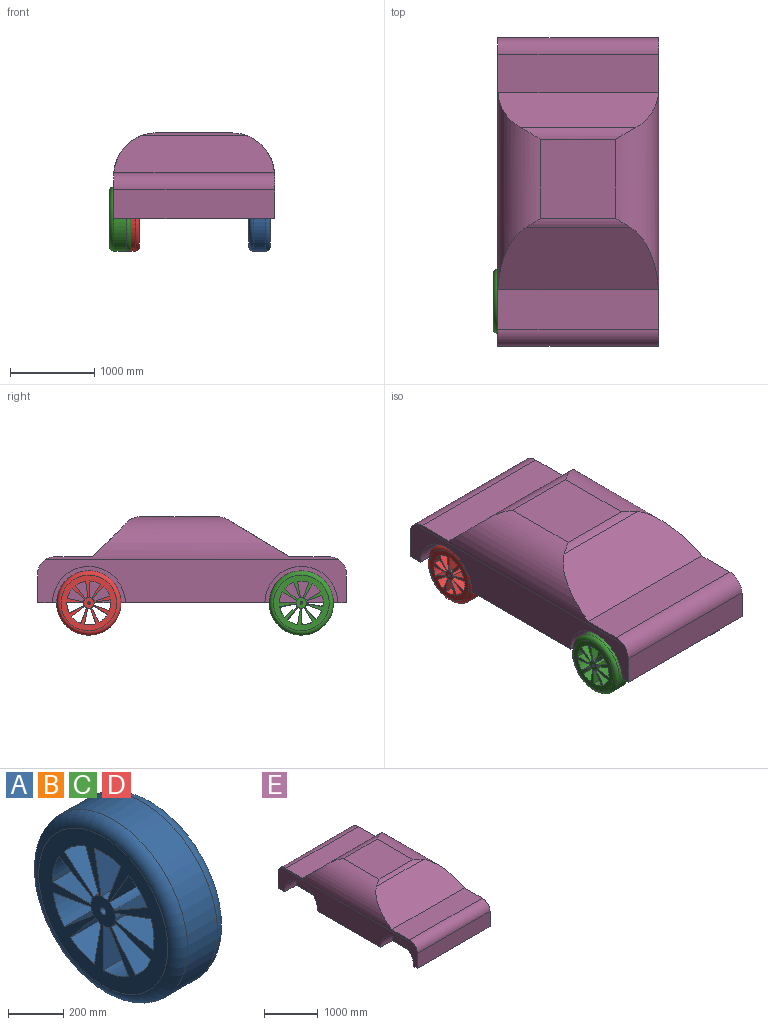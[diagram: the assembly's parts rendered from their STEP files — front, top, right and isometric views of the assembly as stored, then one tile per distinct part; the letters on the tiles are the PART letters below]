
ASSEMBLY  parts=5 mates=9
PART A: 42 faces, bbox 254x824.8x824.8 mm
  f0: plane 660.4x660.4mm, normal (1,0,0), area 191964.8mm2, adj f2,f5,f6,f7,f8,f9,f10,f11
  f1: plane 660.4x660.4mm, normal (-1,0,0), area 191964.8mm2, adj f2,f4,f6,f7,f8,f9,f10,f11
  f2: cylinder r=14.29mm len=254mm, axis (-1,0,0), area 22801.8mm2, adj f0,f1
  f3: cylinder r=381mm len=762mm, axis (-1,0,0), area 364829.4mm2, adj f4,f5
  f4: torus R=330.2mm, axis (1,0,0), area 181769mm2, adj f1,f3
  f5: torus R=330.2mm, axis (1,0,0), area 181769mm2, adj f0,f3
  f6: cylinder r=63.5mm len=254mm, axis (-1,0,0), area 8445.1mm2, adj f0,f1,f7,f9
  f7: plane 254x170.28mm, normal (0,0.5,-0.87), area 49942.1mm2, adj f0,f1,f6,f8
  f8: cylinder r=260.12mm len=254mm, axis (-1,0,0), area 34594.8mm2, adj f0,f1,f7,f9
  f9: plane 254x196.62mm, normal (0,0,1), area 49942.1mm2, adj f0,f1,f6,f8
  f10: plane 254x184.76mm, normal (0,0.94,-0.34), area 49942.1mm2, adj f0,f1,f11,f13
  f11: cylinder r=260.12mm len=254mm, axis (-1,0,0), area 34594.8mm2, adj f0,f1,f10,f12
  f12: plane 254x150.62mm, normal (0,-0.64,0.77), area 49942.1mm2, adj f0,f1,f11,f13
  f13: cylinder r=63.5mm len=254mm, axis (-1,0,0), area 8445.1mm2, adj f0,f1,f10,f12
  f14: cylinder r=63.5mm len=254mm, axis (-1,0,0), area 8445.1mm2, adj f0,f1,f15,f17
  f15: plane 254x193.64mm, normal (0,-0.17,0.98), area 49942.1mm2, adj f0,f1,f14,f16
  f16: cylinder r=260.12mm len=254mm, axis (-1,0,0), area 34594.8mm2, adj f0,f1,f15,f17
  f17: plane 254x184.76mm, normal (0,-0.34,-0.94), area 49942.1mm2, adj f0,f1,f14,f16
  f18: cylinder r=63.5mm len=254mm, axis (-1,0,0), area 8445.1mm2, adj f0,f1,f19,f21
  f19: plane 254x184.76mm, normal (0,0.94,0.34), area 49942.1mm2, adj f0,f1,f18,f20
  f20: cylinder r=260.12mm len=254mm, axis (-1,0,0), area 34594.8mm2, adj f0,f1,f19,f21
  f21: plane 254x193.64mm, normal (0,-0.98,0.17), area 49942.1mm2, adj f0,f1,f18,f20
  f22: cylinder r=63.5mm len=254mm, axis (-1,0,0), area 8445.1mm2, adj f0,f1,f23,f25
  f23: plane 254x170.28mm, normal (0,0.5,0.87), area 49942.1mm2, adj f0,f1,f22,f24
  f24: cylinder r=260.12mm len=254mm, axis (-1,0,0), area 34594.8mm2, adj f0,f1,f23,f25
  f25: plane 254x170.28mm, normal (0,-0.87,-0.5), area 49942.1mm2, adj f0,f1,f22,f24
  f26: cylinder r=63.5mm len=254mm, axis (-1,0,0), area 8445.1mm2, adj f0,f1,f27,f29
  f27: plane 254x196.62mm, normal (0,-1,0), area 49942.1mm2, adj f0,f1,f26,f28
  f28: cylinder r=260.12mm len=254mm, axis (-1,0,0), area 34594.8mm2, adj f0,f1,f27,f29
  f29: plane 254x170.28mm, normal (0,0.87,-0.5), area 49942.1mm2, adj f0,f1,f26,f28
  f30: cylinder r=63.5mm len=254mm, axis (-1,0,0), area 8445.1mm2, adj f0,f1,f31,f33
  f31: plane 254x150.62mm, normal (0,-0.77,0.64), area 49942.1mm2, adj f0,f1,f30,f32
  f32: cylinder r=260.12mm len=254mm, axis (-1,0,0), area 34594.8mm2, adj f0,f1,f31,f33
  f33: plane 254x184.76mm, normal (0,0.34,-0.94), area 49942.1mm2, adj f0,f1,f30,f32
  f34: cylinder r=63.5mm len=254mm, axis (-1,0,0), area 8445.1mm2, adj f0,f1,f35,f37
  f35: plane 254x193.64mm, normal (0,-0.17,-0.98), area 49942.1mm2, adj f0,f1,f34,f36
  f36: cylinder r=260.12mm len=254mm, axis (-1,0,0), area 34594.8mm2, adj f0,f1,f35,f37
  f37: plane 254x150.62mm, normal (0,0.64,0.77), area 49942.1mm2, adj f0,f1,f34,f36
  f38: cylinder r=63.5mm len=254mm, axis (-1,0,0), area 8445.1mm2, adj f0,f1,f39,f41
  f39: plane 254x150.62mm, normal (0,-0.77,-0.64), area 49942.1mm2, adj f0,f1,f38,f40
  f40: cylinder r=260.12mm len=254mm, axis (-1,0,0), area 34594.8mm2, adj f0,f1,f39,f41
  f41: plane 254x193.64mm, normal (0,0.98,0.17), area 49942.1mm2, adj f0,f1,f38,f40
PART B: same geometry as A
PART C: same geometry as A
PART D: same geometry as A
PART E: 24 faces, bbox 1905x3657.6x1019.4 mm
  f0: plane 3657.6x1905mm, normal (0,0,-1), area 5914826.9mm2, adj f1,f2,f3,f4,f10,f11,f12,f13
  f1: plane 3657.6x511.41mm, normal (-1,0,0), area 1275911.3mm2, adj f0,f2,f3,f14,f16,f18,f19,f22
  f2: plane 1905x343.51mm, normal (0,1,0), area 654382.3mm2, adj f0,f1,f4,f18
  f3: plane 1905x343.51mm, normal (0,-1,0), area 654382.3mm2, adj f0,f1,f4,f19
  f4: plane 3657.6x511.41mm, normal (1,0,0), area 1275911.3mm2, adj f0,f2,f3,f10,f12,f18,f19,f23
  f5: plane 1902.54x413.19mm, normal (0,0.71,0.71), area 1014961.6mm2, adj f6,f21,f22,f23
  f6: plane 1902.54x448.77mm, normal (0,0,1), area 853809.5mm2, adj f5,f18,f22,f23
  f7: plane 1902.54x468.47mm, normal (0,0,1), area 891275.6mm2, adj f8,f19,f22,f23
  f8: plane 1902.54x739.57mm, normal (0,-0.51,0.86), area 1472225.8mm2, adj f7,f20,f22,f23
  f9: plane 932.97x889mm, normal (0,0,1), area 829414.3mm2, adj f20,f21,f22,f23
  f10: cylinder r=431.8mm len=863.6mm, axis (1,0,0), area 413473.3mm2, adj f0,f4,f11
  f11: plane 863.6x431.8mm, normal (1,0,0), area 292876.9mm2, adj f0,f10
  f12: cylinder r=431.8mm len=863.6mm, axis (1,0,0), area 413473.3mm2, adj f0,f4,f13
  f13: plane 863.6x431.8mm, normal (1,0,0), area 292876.9mm2, adj f0,f12
  f14: cylinder r=431.8mm len=863.6mm, axis (-1,0,0), area 413473.3mm2, adj f0,f1,f15
  f15: plane 863.6x431.8mm, normal (-1,0,0), area 292876.9mm2, adj f0,f14
  f16: cylinder r=431.8mm len=863.6mm, axis (-1,0,0), area 413473.3mm2, adj f0,f1,f17
  f17: plane 863.6x431.8mm, normal (-1,0,0), area 292876.9mm2, adj f0,f16
  f18: cylinder r=203.2mm len=1905mm, axis (1,0,0), area 607891.2mm2, adj f1,f2,f4,f6,f22,f23
  f19: cylinder r=203.2mm len=1905mm, axis (-1,0,0), area 607891.2mm2, adj f1,f3,f4,f7,f22,f23
  f20: cylinder r=203.2mm len=1227.13mm, axis (1,0,0), area 116438.6mm2, adj f8,f9,f22,f23
  f21: cylinder r=203.2mm len=1366.18mm, axis (1,0,0), area 181038.8mm2, adj f5,f9,f22,f23
  f22: cylinder r=508mm len=3480.11mm, axis (0,1,0), area 1275116.9mm2, adj f1,f5,f6,f7,f8,f9,f18,f19
  f23: cylinder r=508mm len=3480.11mm, axis (0,-1,0), area 1275116.9mm2, adj f4,f5,f6,f7,f8,f9,f18,f19
PLACE A rot(axis=(-1,0,0),41.9deg) t=(1080.08,-997.82,-328.21)mm
PLACE B rot(axis=(0,-0.52,0.85),180deg) t=(1080.08,1519.7,-328.21)mm
PLACE C rot(axis=(1,0,0),0deg) t=(-570.92,-997.82,-328.21)mm
PLACE D rot(axis=(1,0,0),11.6deg) t=(-469.32,1519.7,-328.21)mm
PLACE E t=(305.38,297.31,370.29)mm fixed
MATE cylindrical E.f10 <-> C.f2  axis (-1,0,0) through (-647.12,1519.7,-328.21)mm
MATE planar E.f11 <-> B.f0  axis (1,0,0) through (953.08,1519.7,-144.94)mm
MATE planar E.f17 <-> D.f0  axis (-1,0,0) through (-342.32,-997.82,-144.94)mm
MATE cylindrical E.f12 <-> C.f2  axis (-1,0,0) through (-494.72,-997.82,-328.21)mm
MATE cylindrical E.f10 <-> B.f2  axis (1,0,0) through (1105.48,1519.7,-328.21)mm
MATE cylindrical E.f10 <-> D.f2  axis (-1,0,0) through (-494.72,1519.7,-328.21)mm
MATE cylindrical E.f12 <-> C.f2  axis (-1,0,0) through (-494.72,-997.82,-328.21)mm
MATE cylindrical E.f12 <-> A.f2  axis (1,0,0) through (1105.48,-997.82,-328.21)mm
MATE planar E.f13 <-> A.f1  axis (1,0,0) through (953.08,-997.82,-144.94)mm
